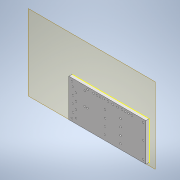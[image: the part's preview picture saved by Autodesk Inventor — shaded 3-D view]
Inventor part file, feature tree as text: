
AUTODESK INVENTOR PART (.ipt)
format: ipt  version: 2021 (Build 250183000, 183)  size: 456,704 bytes
history: native  units: in
note: dims shown in document units (in); Inventor stores cm internally (conversion verified against a paired STEP export)
features: reference x60, projected_geometry x16, other x10, extrude x3, hole x3, sketch x2, plane x1
ambient origin geometry x8: Origin, YZ Plane, XZ Plane, XY Plane, X Axis, Y Axis, Z Axis, Center Point
bodies: Solid1 (feature_tree)
feature tree (95):
  extrude  "Extrusion base plate"  [1 undecoded]
  plane  "work plane for rib creation"
  other  "channels as rib"
  extrude  "extrusion of ribs to get cutout"  Depth=0.1181in
  extrude  "valve space extrusion"  Depth=0.9055in
  other  "all valve spaces"
  other  "projected points for every hole for control layer only"
  hole  "holes for control layer"  [1 undecoded]
  other  "projected points for every hole for flow layer only"
  hole  "holes for connection to flow layer"  [1 undecoded]
  hole  "holes in corners"  [1 undecoded]
  other  "all holes for flow layer only"
  sketch  "Sketch1"  dims[d2=0.315in d3=0.0in d4=-0.0394in]
  other  "channels and points for valves and for connectors for control layer"
  reference  "Reference1"
  reference  "Reference2"
  reference  "Reference3"
  reference  "Reference4"
  reference  "Reference5"
  reference  "Reference6"
  reference  "Reference7"
  reference  "Reference8"
  reference  "Reference9"
  reference  "Reference10"
  reference  "Reference11"
  reference  "Reference12"
  reference  "Reference13"
  reference  "Reference14"
  reference  "Reference15"
  reference  "Reference16"
  reference  "Reference17"
  reference  "Reference18"
  reference  "Reference19"
  reference  "Reference20"
  reference  "Reference21"
  reference  "Reference22"
  reference  "Reference23"
  reference  "Reference24"
  reference  "Reference25"
  reference  "Reference26"
  reference  "Reference27"
  reference  "Reference28"
  reference  "Reference29"
  reference  "Reference30"
  reference  "Reference31"
  reference  "Reference32"
  reference  "Reference33"
  reference  "Reference34"
  reference  "Reference35"
  sketch  "Sketch3"  dims[d5=7.874in d6=11.811in d7=0.9055in d8=3.4252in d9=0.3543in d10=0.3543in d11=0.3543in d12=0.3543in d19=0.0157in d20=0.0394in d21=0.0in d22=0.0in d23=0.0394in d24=0.0in d25=0.0787in d26=0.0in d27=0.0394in d28=0.0in d29=0.1575in d30=0.2362in d31=0.1575in d32=0.0787in d33=90.0deg d34=0.0394in d35=0.0in d36=0.1575in d37=0.2362in d38=0.1575in d39=0.0787in d40=90.0deg d41=0.0394in d42=0.0in d43=0.1575in d44=0.2362in d45=0.1575in d46=0.0787in d47=90.0deg d48=0.315in d49=0.8108in d50=0.1181in d51=0.0886in]
  projected_geometry  "Projected Loop1"
  projected_geometry  "Projected Loop2"
  projected_geometry  "Projected Loop3"
  projected_geometry  "Projected Loop4"
  projected_geometry  "Projected Loop5"
  projected_geometry  "Projected Loop6"
  projected_geometry  "Projected Loop7"
  projected_geometry  "Projected Loop8"
  projected_geometry  "Projected Loop9"
  projected_geometry  "Projected Loop10"
  projected_geometry  "Projected Loop11"
  projected_geometry  "Projected Loop12"
  projected_geometry  "Projected Loop13"
  projected_geometry  "Projected Loop14"
  projected_geometry  "Projected Loop15"
  projected_geometry  "Projected Loop16"
  reference  "Reference36"
  other  "Projected points for every valve"
  reference  "Reference37"
  reference  "Reference38"
  reference  "Reference39"
  reference  "Reference40"
  reference  "Reference41"
  reference  "Reference42"
  reference  "Reference43"
  reference  "Reference44"
  reference  "Reference45"
  reference  "Reference46"
  reference  "Reference47"
  reference  "Reference48"
  reference  "Reference49"
  reference  "Reference50"
  reference  "Reference51"
  reference  "Reference52"
  reference  "Reference53"
  reference  "Reference54"
  reference  "Reference55"
  reference  "Reference56"
  other  "projection for holes in corners"
  reference  "Reference57"
  reference  "Reference58"
  reference  "Reference59"
  reference  "Reference60"
  other  "Millifluidic Board.iam"
  other  "Flow Layer:1"
note: 4 required parameter values undecoded (feature->parameter linkage not recoverable at this tier; creation-order binding heuristic only, values carry confidence <= 0.55)
